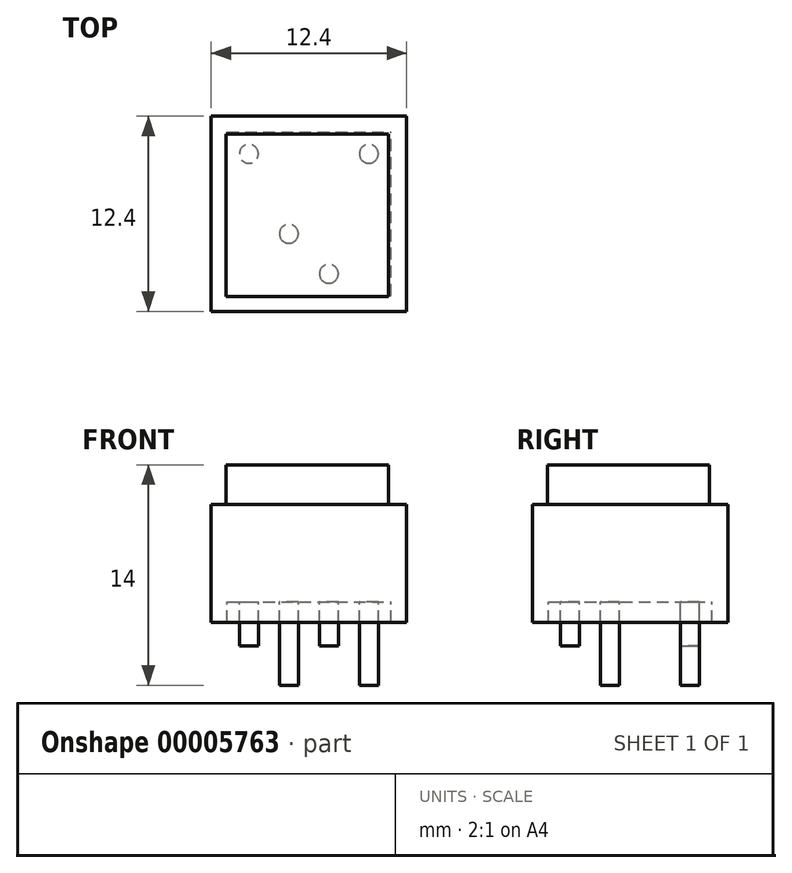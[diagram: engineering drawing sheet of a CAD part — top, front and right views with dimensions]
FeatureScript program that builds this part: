
annotation { "Feature Type Name" : "Feature", "Feature Type Description" : "" }
export const myFeature = defineFeature(function(context is Context, id is Id, definition is map)
    precondition{}
    {
        {
            var Q0;
            Q0=qCreatedBy(makeId("Top.planeOp"),FACE);
            var sketch = newSketch(context, id + "F0", { "sketchPlane" : qUnion([Q0])});
            skLineSegment(sketch, "E0.bottom", {"start": v(0, 0) * mm, "end": v(12.4, 0) * mm});
            skLineSegment(sketch, "E0.top", {"start": v(0, -12.4) * mm, "end": v(12.4, -12.4) * mm});
            skLineSegment(sketch, "E0.left", {"start": v(0, 0) * mm, "end": v(0, -12.4) * mm});
            skLineSegment(sketch, "E0.right", {"start": v(12.4, 0) * mm, "end": v(12.4, -12.4) * mm});
            skSolve(sketch);
        }
        {
            var Q0;
            Q0=makeQuery(id+"F0.imprint","IMPRINT",FACE,{"disambiguationData":[TD([[makeQuery(id+"F0.imprint","IMPRINT",EDGE,{"derivedFrom":sQuery(id+"F0.wireOp",EDGE,"E0.bottom")}),-1.0]])]});
            extrude(context, id + "F1", {"entities" : qUnion([Q0]), "depth" : 6.2 * mm});
        }
        {
            var Q0;
            Q0=makeQuery(id+"F1.opExtrude","CAP_FACE",FACE,{"disambiguationData":[OSD([sQuery(id+"F0.wireOp",EDGE,"E0.bottom"),sQuery(id+"F0.wireOp",EDGE,"E0.top"),sQuery(id+"F0.wireOp",EDGE,"E0.left"),sQuery(id+"F0.wireOp",EDGE,"E0.right")])],"isStart":true});
            var sketch = newSketch(context, id + "F2", { "sketchPlane" : qUnion([Q0])});
            skLineSegment(sketch, "E1.bottom", {"start": v(0, 12.4) * mm, "end": v(12.4, 12.4) * mm});
            skLineSegment(sketch, "E1.top", {"start": v(0, 0) * mm, "end": v(12.4, 0) * mm});
            skLineSegment(sketch, "E1.left", {"start": v(0, 12.4) * mm, "end": v(0, 0) * mm});
            skLineSegment(sketch, "E1.right", {"start": v(12.4, 12.4) * mm, "end": v(12.4, 0) * mm});
            skLineSegment(sketch, "E2.bottom", {"start": v(1, 11.4) * mm, "end": v(11.4, 11.4) * mm});
            skLineSegment(sketch, "E2.top", {"start": v(1, 1) * mm, "end": v(11.4, 1) * mm});
            skLineSegment(sketch, "E2.left", {"start": v(1, 11.4) * mm, "end": v(1, 1) * mm});
            skLineSegment(sketch, "E2.right", {"start": v(11.4, 11.4) * mm, "end": v(11.4, 1) * mm});
            skSolve(sketch);
        }
        {
            var Q0;
            Q0=makeQuery(id+"F1.opExtrude","CAP_FACE",FACE,{"disambiguationData":[OSD([sQuery(id+"F0.wireOp",EDGE,"E0.bottom"),sQuery(id+"F0.wireOp",EDGE,"E0.top"),sQuery(id+"F0.wireOp",EDGE,"E0.left"),sQuery(id+"F0.wireOp",EDGE,"E0.right")])],"isStart":false});
            var sketch = newSketch(context, id + "F3", { "sketchPlane" : qUnion([Q0])});
            skLineSegment(sketch, "E3.bottom", {"start": v(0.95, -1.15) * mm, "end": v(11.25, -1.15) * mm});
            skLineSegment(sketch, "E3.top", {"start": v(0.95, -11.45) * mm, "end": v(11.25, -11.45) * mm});
            skLineSegment(sketch, "E3.left", {"start": v(0.95, -1.15) * mm, "end": v(0.95, -11.45) * mm});
            skLineSegment(sketch, "E3.right", {"start": v(11.25, -1.15) * mm, "end": v(11.25, -11.45) * mm});
            skSolve(sketch);
        }
        {
            var Q0;
            Q0=qSketchRegion(id+"F3",true);
            extrude(context, id + "F4", {"entities" : qUnion([Q0]), "depth" : 2.5 * mm});
        }
        {
            var Q0;
            Q0=makeQuery(id+"F1.opExtrude","CAP_FACE",FACE,{"disambiguationData":[OSD([sQuery(id+"F0.wireOp",EDGE,"E0.bottom"),sQuery(id+"F0.wireOp",EDGE,"E0.top"),sQuery(id+"F0.wireOp",EDGE,"E0.left"),sQuery(id+"F0.wireOp",EDGE,"E0.right")])],"isStart":true});
            var sketch = newSketch(context, id + "F5", { "sketchPlane" : qUnion([Q0])});
            skCircle(sketch, "E4", {"center": v(2.4, 2.39) * mm, "radius": 0.6 * mm});
            skSolve(sketch);
        }
        {
            var Q0;
            Q0=qSketchRegion(id+"F5",true);
            extrude(context, id + "F6", {"entities" : qUnion([Q0]), "operationType" : NewBodyOperationType.ADD, "depth" : 2.8 * mm});
        }
        {
            var Q0;
            Q0=makeQuery(id+"F1.opExtrude","CAP_FACE",FACE,{"disambiguationData":[OSD([sQuery(id+"F0.wireOp",EDGE,"E0.bottom"),sQuery(id+"F0.wireOp",EDGE,"E0.top"),sQuery(id+"F0.wireOp",EDGE,"E0.left"),sQuery(id+"F0.wireOp",EDGE,"E0.right")])],"isStart":true});
            var sketch = newSketch(context, id + "F7", { "sketchPlane" : qUnion([Q0])});
            skCircle(sketch, "E5", {"center": v(7.47, 10) * mm, "radius": 0.6 * mm});
            skSolve(sketch);
        }
        {
            var Q0;
            Q0=qSketchRegion(id+"F7",true);
            extrude(context, id + "F8", {"entities" : qUnion([Q0]), "operationType" : NewBodyOperationType.ADD, "depth" : 2.8 * mm});
        }
        {
            var Q0;
            Q0=makeQuery(id+"F1.opExtrude","CAP_FACE",FACE,{"disambiguationData":[OSD([sQuery(id+"F0.wireOp",EDGE,"E0.bottom"),sQuery(id+"F0.wireOp",EDGE,"E0.top"),sQuery(id+"F0.wireOp",EDGE,"E0.left"),sQuery(id+"F0.wireOp",EDGE,"E0.right")])],"isStart":true});
            var sketch = newSketch(context, id + "F9", { "sketchPlane" : qUnion([Q0])});
            skCircle(sketch, "E6", {"center": v(10, 2.4) * mm, "radius": 0.6 * mm});
            skSolve(sketch);
        }
        {
            var Q0;
            Q0=qSketchRegion(id+"F9",true);
            extrude(context, id + "F10", {"entities" : qUnion([Q0]), "operationType" : NewBodyOperationType.ADD, "depth" : 5.3 * mm});
        }
        {
            var Q0;
            Q0=makeQuery(id+"F1.opExtrude","CAP_FACE",FACE,{"disambiguationData":[OSD([sQuery(id+"F0.wireOp",EDGE,"E0.bottom"),sQuery(id+"F0.wireOp",EDGE,"E0.top"),sQuery(id+"F0.wireOp",EDGE,"E0.left"),sQuery(id+"F0.wireOp",EDGE,"E0.right")])],"isStart":true});
            var sketch = newSketch(context, id + "F11", { "sketchPlane" : qUnion([Q0])});
            skCircle(sketch, "E7", {"center": v(4.93, 7.47) * mm, "radius": 0.6 * mm});
            skSolve(sketch);
        }
        {
            var Q0;
            Q0=qSketchRegion(id+"F11",true);
            extrude(context, id + "F12", {"entities" : qUnion([Q0]), "operationType" : NewBodyOperationType.ADD, "depth" : 5.3 * mm});
        }
        {
            var Q0;
            Q0=qSketchRegion(id+"F2",true);
            extrude(context, id + "F13", {"entities" : qUnion([Q0]), "operationType" : NewBodyOperationType.ADD, "depth" : 1.3 * mm});
        }
    });
